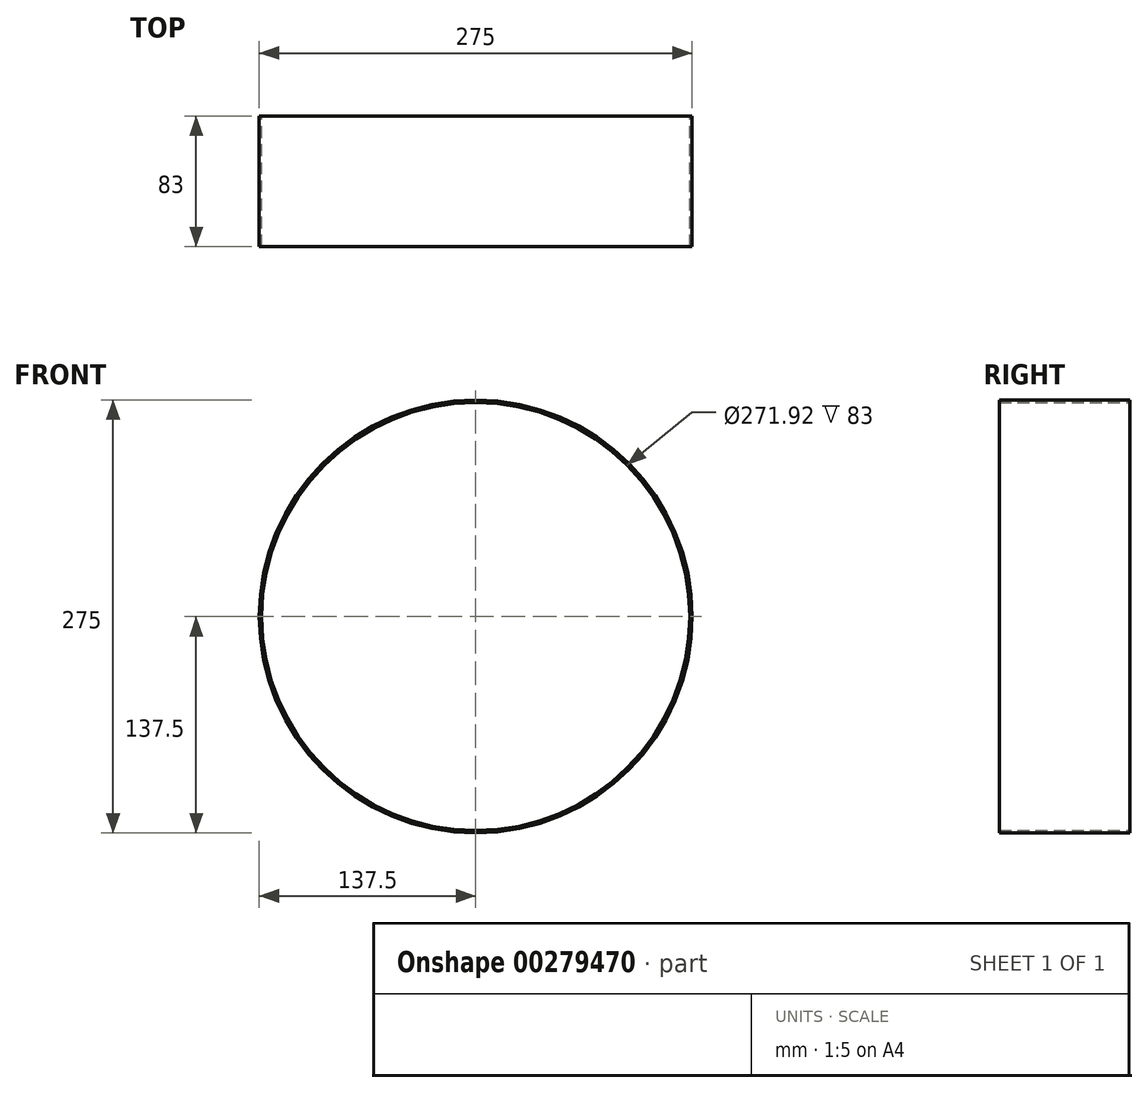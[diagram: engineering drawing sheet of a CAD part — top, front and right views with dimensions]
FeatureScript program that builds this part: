
annotation { "Feature Type Name" : "Feature", "Feature Type Description" : "" }
export const myFeature = defineFeature(function(context is Context, id is Id, definition is map)
    precondition{}
    {
        {
            var Q0;
            Q0=qCreatedBy(makeId("Front.planeOp"),FACE);
            var sketch = newSketch(context, id + "F0", { "sketchPlane" : qUnion([Q0])});
            skCircle(sketch, "E0", {"center": v(0, 0) * mm, "radius": 137.5 * mm});
            skCircle(sketch, "E1", {"center": v(0, 0) * mm, "radius": 135.96 * mm});
            skSolve(sketch);
        }
        {
            var Q0;
            Q0=qSketchRegion(id+"F0",true);
            extrude(context, id + "F1", {"entities" : qUnion([Q0]), "depth" : 3 * mm});
        }
        {
            var Q0;
            Q0=makeQuery(id+"F1.opExtrude","CAP_FACE",FACE,{"disambiguationData":[OSD([sQuery(id+"F0.wireOp",EDGE,"E0"),sQuery(id+"F0.wireOp",EDGE,"E1")])],"isStart":false});
            var Q1;
            Q1=makeQuery(id+"F1.opExtrude","CAP_FACE",FACE,{"disambiguationData":[OSD([sQuery(id+"F0.wireOp",EDGE,"E0"),sQuery(id+"F0.wireOp",EDGE,"E1")])],"isStart":true});
            extrude(context, id + "F2", {"entities" : qUnion([Q0, Q1]), "operationType" : NewBodyOperationType.ADD, "depth" : 80 * mm, "offsetDistance" : 25 * mm});
        }
    });
